# Revit family: 10600800
name_source: partatom
category: Specialty Equipment
units: mm (PartAtom-declared; Revit-internal decimal feet)

## family parameters
Always vertical = Yes
Cut with Voids When Loaded = No
Enable Cutting in Views = Yes
Maintain Annotation Orientation = No
OmniClass Number = 23.40.40.00
OmniClass Title = Food Service Equipment and Furnishings
Part Type = Normal
Room Calculation Point = No
Round Connector Dimension = Use Diameter
Shared = No
Work Plane-Based = No

## types (1)
- Standard
    3D-Driven = Yes
    Default Elevation = 0 mm  [stored 0 ft]
    Description = Serveringsdisk RBRM-800
    Design State = 1
    Manufacturer = Rustfriebergh AS
    Model = 10600800
    Part Number = 10600800
    Revision Number = -
    SoveliaReference = Yes
    URL = https://www.rustfriebergh.no

note: [stored X ft] marks values corroborated as IEEE doubles in the binary element streams (Revit-internal decimal feet)

## geometry (parser evidence)
native form markers: Sweep x3
no freeform markers — native parametric forms only
